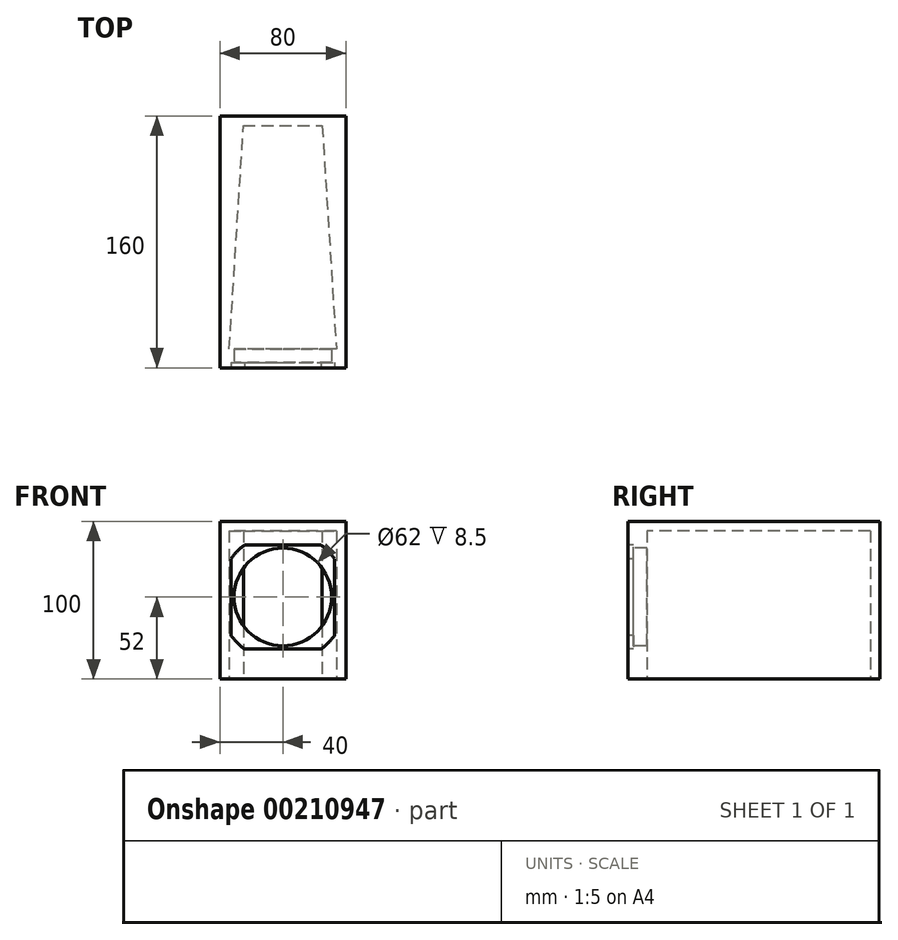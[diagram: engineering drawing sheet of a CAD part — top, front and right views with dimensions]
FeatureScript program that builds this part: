
annotation { "Feature Type Name" : "Feature", "Feature Type Description" : "" }
export const myFeature = defineFeature(function(context is Context, id is Id, definition is map)
    precondition{}
    {
        {
            var Q0;
            Q0=qCreatedBy(makeId("Top.planeOp"),FACE);
            var sketch = newSketch(context, id + "F0", { "sketchPlane" : qUnion([Q0])});
            skLineSegment(sketch, "E0.bottom", {"start": v(-40, 95) * mm, "end": v(40, 95) * mm});
            skLineSegment(sketch, "E0.top", {"start": v(-40, -65) * mm, "end": v(40, -65) * mm});
            skLineSegment(sketch, "E0.left", {"start": v(-40, 95) * mm, "end": v(-40, -65) * mm});
            skLineSegment(sketch, "E0.right", {"start": v(40, 95) * mm, "end": v(40, -65) * mm});
            skSolve(sketch);
        }
        {
            var Q0;
            Q0 = qSketchRegion(id + "F0", true);
            extrude(context, id + "F1", {"entities" : qUnion([Q0]), "depth" : 100 * mm});
        }
        {
            var Q0;
            Q0=makeQuery(id+"F1.opExtrude","CAP_FACE",FACE,{"disambiguationData":[OSD([sQuery(id+"F0.wireOp",EDGE,"E0.bottom"),sQuery(id+"F0.wireOp",EDGE,"E0.top"),sQuery(id+"F0.wireOp",EDGE,"E0.left"),sQuery(id+"F0.wireOp",EDGE,"E0.right")])],"isStart":true});
            var sketch = newSketch(context, id + "F2", { "sketchPlane" : qUnion([Q0])});
            skLineSegment(sketch, "E1", {"start": v(25, -89) * mm, "end": v(34, 53) * mm});
            skLineSegment(sketch, "E2", {"start": v(34, 53) * mm, "end": v(-34, 53) * mm});
            skLineSegment(sketch, "E3", {"start": v(-34, 53) * mm, "end": v(-25, -89) * mm});
            skLineSegment(sketch, "E4", {"start": v(-25, -89) * mm, "end": v(25, -89) * mm});
            skSolve(sketch);
        }
        {
            var Q0;
            Q0 = qSketchRegion(id + "F2", true);
            extrude(context, id + "F3", {"entities" : qUnion([Q0]), "operationType" : NewBodyOperationType.REMOVE, "oppositeDirection" : true, "depth" : 94 * mm});
        }
        {
            var Q0;
            Q0=makeQuery(id+"F1.opExtrude","SWEPT_FACE",FACE,{"disambiguationData":[OSD([sQuery(id+"F0.wireOp",EDGE,"E0.top")])]});
            var sketch = newSketch(context, id + "F4", { "sketchPlane" : qUnion([Q0])});
            skArc(sketch, "E5", {"start": v(-24.33, 85) * mm, "mid": v(-29, 81) * mm, "end": v(-33, 76.33) * mm});
            skArc(sketch, "E6", {"start": v(33, 27.67) * mm, "mid": v(29, 23) * mm, "end": v(24.33, 19) * mm});
            skArc(sketch, "E7", {"start": v(24.33, 85) * mm, "mid": v(29, 81) * mm, "end": v(33, 76.33) * mm});
            skArc(sketch, "E8", {"start": v(-24.33, 19) * mm, "mid": v(-29, 23) * mm, "end": v(-33, 27.67) * mm});
            skLineSegment(sketch, "E9", {"start": v(-33, 76.33) * mm, "end": v(-33, 27.67) * mm});
            skLineSegment(sketch, "E10", {"start": v(-24.33, 19) * mm, "end": v(24.33, 19) * mm});
            skLineSegment(sketch, "E11", {"start": v(33, 27.67) * mm, "end": v(33, 76.33) * mm});
            skLineSegment(sketch, "E12", {"start": v(24.33, 85) * mm, "end": v(-24.33, 85) * mm});
            skSolve(sketch);
        }
        {
            var Q0;
            Q0 = qSketchRegion(id + "F4", true);
            extrude(context, id + "F5", {"entities" : qUnion([Q0]), "operationType" : NewBodyOperationType.REMOVE, "oppositeDirection" : true, "depth" : 3.5 * mm});
        }
        {
            var Q0;
            Q0=makeQuery(id+"F5.boolean.opBoolean","COPY",FACE,{"derivedFrom":makeQuery(id+"F5.opExtrude","CAP_FACE",FACE,{"disambiguationData":[OSD([sQuery(id+"F4.wireOp",EDGE,"E5"),sQuery(id+"F4.wireOp",EDGE,"E6"),sQuery(id+"F4.wireOp",EDGE,"E7"),sQuery(id+"F4.wireOp",EDGE,"E8"),sQuery(id+"F4.wireOp",EDGE,"E9"),sQuery(id+"F4.wireOp",EDGE,"E10"),sQuery(id+"F4.wireOp",EDGE,"E11"),sQuery(id+"F4.wireOp",EDGE,"E12")])],"isStart":false})});
            var sketch = newSketch(context, id + "F6", { "sketchPlane" : qUnion([Q0])});
            skCircle(sketch, "E13", {"center": v(0, 52) * mm, "radius": 31 * mm});
            skSolve(sketch);
        }
        {
            var Q0;
            Q0 = qSketchRegion(id + "F6", true);
            extrude(context, id + "F7", {"entities" : qUnion([Q0]), "operationType" : NewBodyOperationType.REMOVE, "oppositeDirection" : true, "depth" : 25 * mm});
        }
        {
            var Q0;
            Q0=makeQuery(id+"F1.opExtrude","SWEPT_BODY",BODY,{"disambiguationData":[OSD([sQuery(id+"F0.wireOp",EDGE,"E0.bottom"),sQuery(id+"F0.wireOp",EDGE,"E0.top"),sQuery(id+"F0.wireOp",EDGE,"E0.left"),sQuery(id+"F0.wireOp",EDGE,"E0.right")])]});
            var Q1;
            Q1=makeQuery(id+"F1.opExtrude","CAP_EDGE",EDGE,{"disambiguationData":[OSD([sQuery(id+"F0.wireOp",EDGE,"E0.right")])],"isStart":true});
            transform(context, id + "F8", {"entities" : qUnion([Q0]), "transformType" : TransformType.ROTATION, "transformAxis" : qUnion([Q1]), "angle" : 180 * degree, "makeCopy" : true});
        }
        {
            var Q0;
            Q0=makeQuery(id+"F8.opPattern","COPY",BODY,{"derivedFrom":makeQuery(id+"F1.opExtrude","SWEPT_BODY",BODY,{"disambiguationData":[OSD([sQuery(id+"F0.wireOp",EDGE,"E0.bottom"),sQuery(id+"F0.wireOp",EDGE,"E0.top"),sQuery(id+"F0.wireOp",EDGE,"E0.left"),sQuery(id+"F0.wireOp",EDGE,"E0.right")])]}),"instanceName":"1"});
            deleteBodies(context, id + "F9", {"entities" : qUnion([Q0])});
        }
    });
